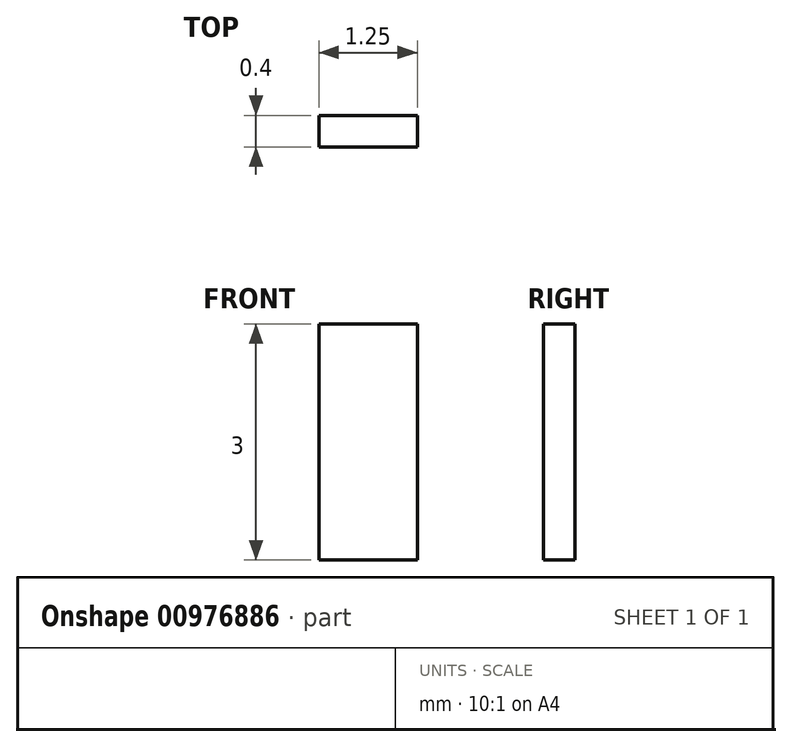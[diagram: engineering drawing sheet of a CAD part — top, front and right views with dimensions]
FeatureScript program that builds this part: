
annotation { "Feature Type Name" : "Feature", "Feature Type Description" : "" }
export const myFeature = defineFeature(function(context is Context, id is Id, definition is map)
    precondition{}
    {
        {
            var Q0;
            Q0=qCreatedBy(makeId("Front.planeOp"),FACE);
            var sketch = newSketch(context, id + "F0", { "sketchPlane" : qUnion([Q0])});
            skLineSegment(sketch, "E0", {"start": v(-0.74, 10.1) * mm, "end": v(0.5, 10.1) * mm});
            skLineSegment(sketch, "E1", {"start": v(0.5, 10.1) * mm, "end": v(0.5, 13.1) * mm});
            skLineSegment(sketch, "E2", {"start": v(0.5, 13.1) * mm, "end": v(-0.74, 13.1) * mm});
            skLineSegment(sketch, "E3", {"start": v(-0.74, 13.1) * mm, "end": v(-0.74, 10.1) * mm});
            skSolve(sketch);
        }
        {
            var Q0;
            Q0 = qSketchRegion(id + "F0", true);
            extrude(context, id + "F1", {"entities" : qUnion([Q0]), "depth" : 0.4 * mm, "offsetDistance" : 25 * mm});
        }
    });
